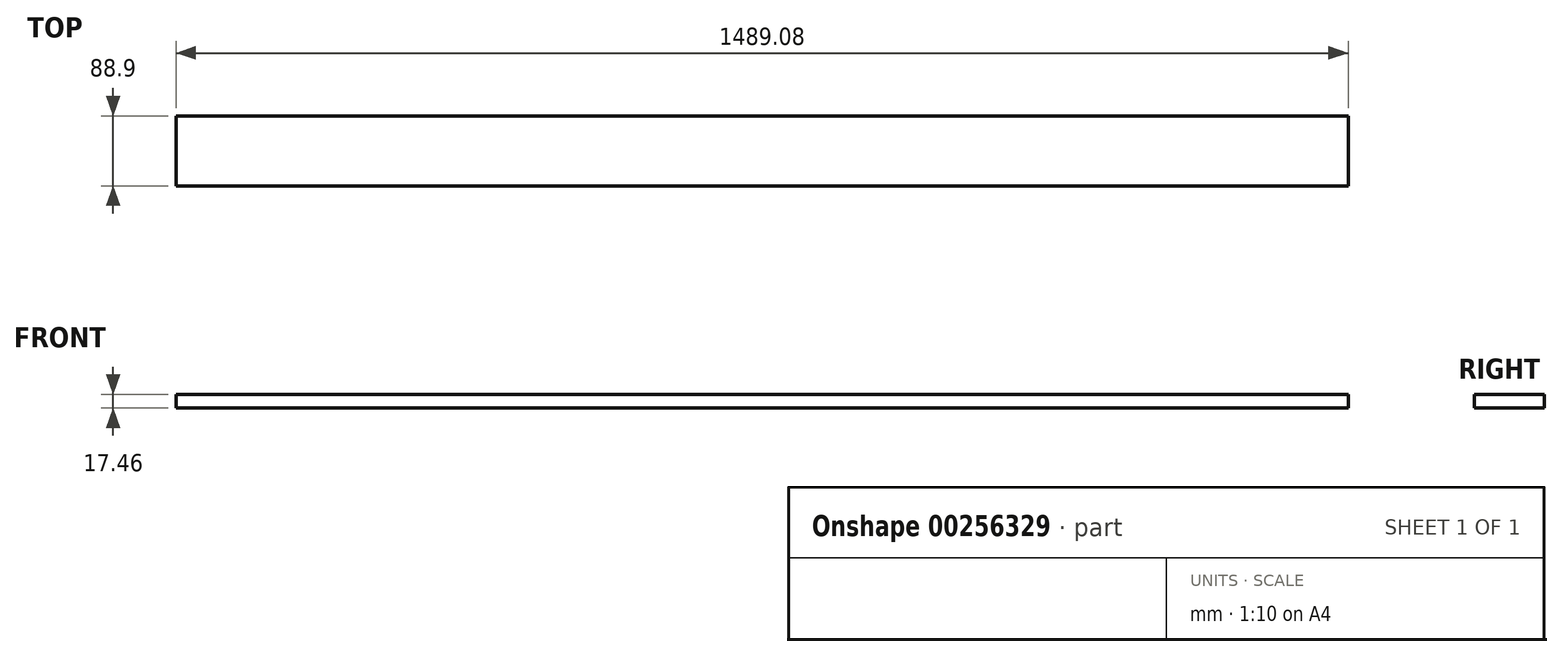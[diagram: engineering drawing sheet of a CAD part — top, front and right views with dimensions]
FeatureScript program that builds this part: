
annotation { "Feature Type Name" : "Feature", "Feature Type Description" : "" }
export const myFeature = defineFeature(function(context is Context, id is Id, definition is map)
    precondition{}
    {
        {
            var Q0;
            Q0=qCreatedBy(makeId("Right.planeOp"),FACE);
            var sketch = newSketch(context, id + "F0", { "sketchPlane" : qUnion([Q0])});
            skLineSegment(sketch, "E0.bottom", {"start": v(-44.45, 8.73) * mm, "end": v(44.45, 8.73) * mm});
            skLineSegment(sketch, "E0.top", {"start": v(-44.45, -8.73) * mm, "end": v(44.45, -8.73) * mm});
            skLineSegment(sketch, "E0.left", {"start": v(-44.45, 8.73) * mm, "end": v(-44.45, -8.73) * mm});
            skLineSegment(sketch, "E0.right", {"start": v(44.45, 8.73) * mm, "end": v(44.45, -8.73) * mm});
            skSolve(sketch);
        }
        {
            var Q0;
            Q0=qSketchRegion(id+"F0",true);
            extrude(context, id + "F1", {"entities" : qUnion([Q0]), "endBound" : BoundingType.SYMMETRIC, "depth" : 1489.07 * mm});
        }
    });
